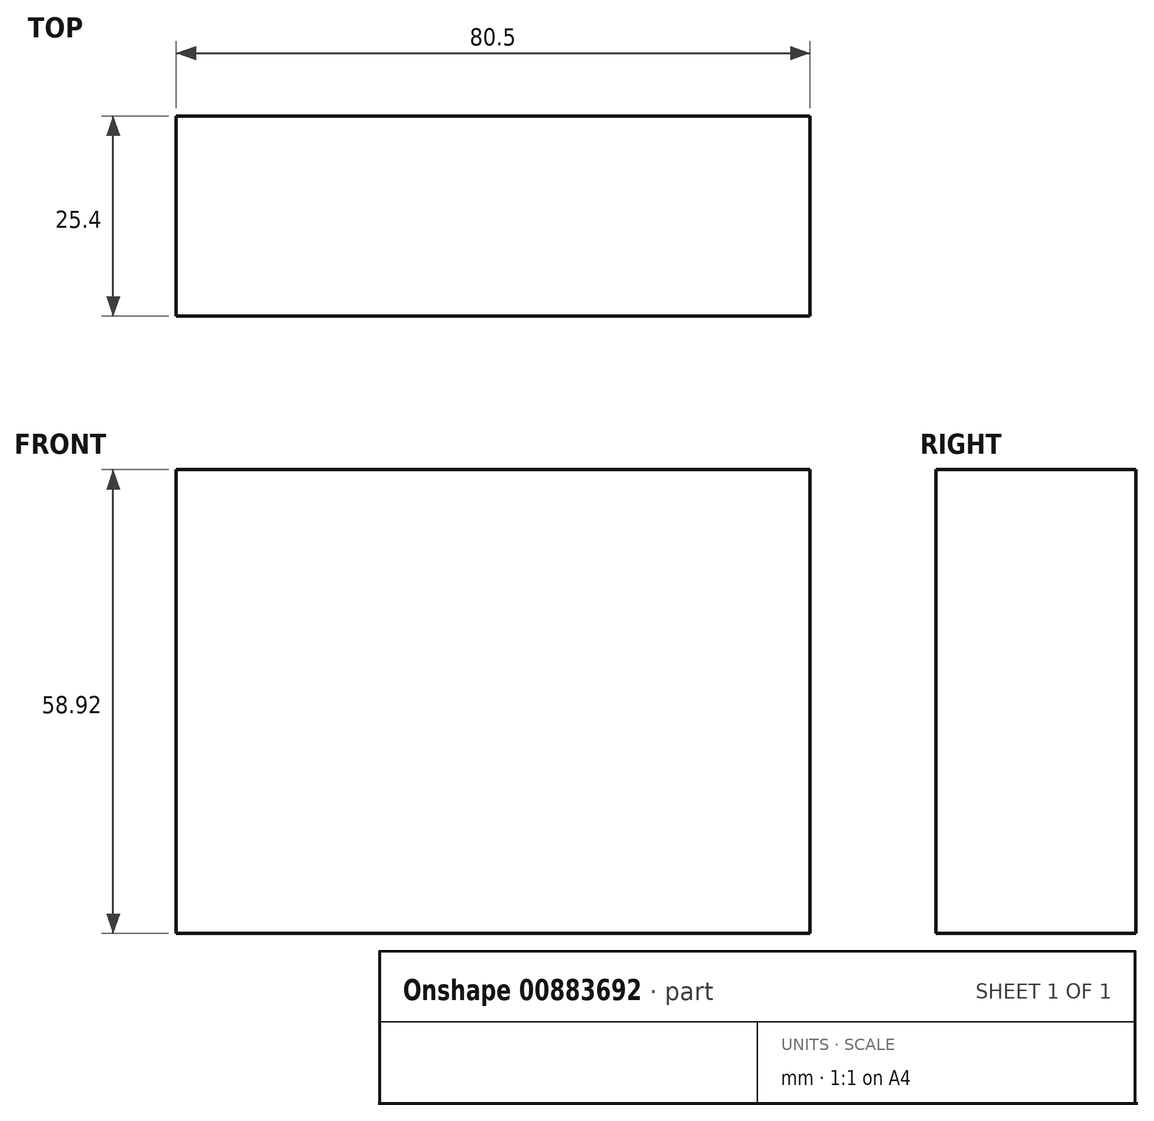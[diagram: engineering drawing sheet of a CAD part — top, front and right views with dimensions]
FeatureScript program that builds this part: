
annotation { "Feature Type Name" : "Feature", "Feature Type Description" : "" }
export const myFeature = defineFeature(function(context is Context, id is Id, definition is map)
    precondition{}
    {
        {
            var Q0;
            Q0=qCreatedBy(makeId("Front.planeOp"),FACE);
            var sketch = newSketch(context, id + "F0", { "sketchPlane" : qUnion([Q0])});
            skLineSegment(sketch, "E0.bottom", {"start": v(40.25, 29.46) * mm, "end": v(-40.25, 29.46) * mm});
            skLineSegment(sketch, "E0.top", {"start": v(40.25, -29.46) * mm, "end": v(-40.25, -29.46) * mm});
            skLineSegment(sketch, "E0.left", {"start": v(40.25, 29.46) * mm, "end": v(40.25, -29.46) * mm});
            skLineSegment(sketch, "E0.right", {"start": v(-40.25, 29.46) * mm, "end": v(-40.25, -29.46) * mm});
            skPoint(sketch, "E0.middle", {"position": v(0, 0) * mm});
            skSolve(sketch);
        }
        {
            var Q0;
            Q0=makeQuery(id+"F0.imprint","IMPRINT",FACE,{"disambiguationData":[TD([[makeQuery(id+"F0.imprint","IMPRINT",EDGE,{"derivedFrom":sQuery(id+"F0.wireOp",EDGE,"E0.bottom")}),1.0]])]});
            extrude(context, id + "F1", {"entities" : qUnion([Q0]), "depth" : 25.4 * mm, "offsetDistance" : 25.4 * mm});
        }
        {
            var Q0;
            Q0=qCreatedBy(makeId("Front.planeOp"),FACE);
            var sketch = newSketch(context, id + "F2", { "sketchPlane" : qUnion([Q0])});
            skEllipse(sketch, "E1", {"center": v(9.96, 9.54) * mm, "majorRadius": 22.95 * mm, "minorRadius": 14.5 * mm, "majorAxis": v(-1, 0)});
            skSolve(sketch);
        }
        {
            var Q0;
            Q0=sQuery(id+"F2.wireOp",EDGE,"E1");
            extrude(context, id + "F3", {"bodyType" : ToolBodyType.SURFACE, "surfaceEntities" : qUnion([Q0]), "endBound" : BoundingType.THROUGH_ALL, "depth" : 50.8 * mm, "offsetDistance" : 25.4 * mm});
        }
    });
